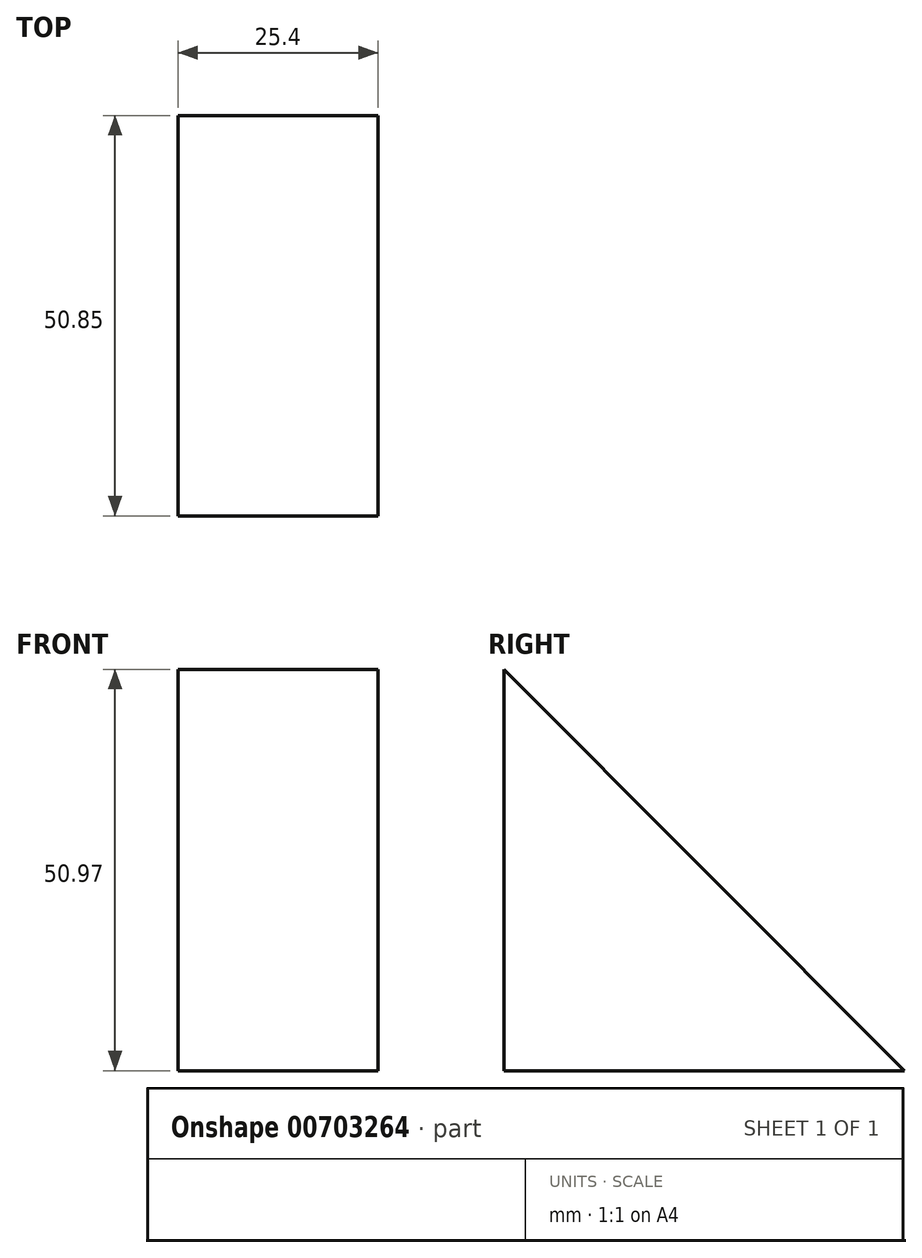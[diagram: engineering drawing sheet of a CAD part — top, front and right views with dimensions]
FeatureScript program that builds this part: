
annotation { "Feature Type Name" : "Feature", "Feature Type Description" : "" }
export const myFeature = defineFeature(function(context is Context, id is Id, definition is map)
    precondition{}
    {
        {
            var Q0;
            Q0=qCreatedBy(makeId("Right.planeOp"),FACE);
            var sketch = newSketch(context, id + "F0", { "sketchPlane" : qUnion([Q0])});
            skLineSegment(sketch, "E0", {"start": v(0, 0) * mm, "end": v(-50.85, 0) * mm});
            skLineSegment(sketch, "E1", {"start": v(-50.85, 0) * mm, "end": v(-50.85, 50.97) * mm});
            skLineSegment(sketch, "E2", {"start": v(-50.85, 50.97) * mm, "end": v(0, 0) * mm});
            skLineSegment(sketch, "E3", {"start": v(0, 0) * mm, "end": v(21.7, 0) * mm});
            skLineSegment(sketch, "E4", {"start": v(21.7, 0) * mm, "end": v(13.56, 0) * mm});
            skLineSegment(sketch, "E5", {"start": v(13.56, 0) * mm, "end": v(21.7, 0) * mm});
            skSolve(sketch);
        }
        {
            var Q0;
            Q0=makeQuery(id+"F0.imprint","IMPRINT",FACE,{"disambiguationData":[TD([[makeQuery(id+"F0.imprint","IMPRINT",EDGE,{"derivedFrom":sQuery(id+"F0.wireOp",EDGE,"E0")}),-1.0]])]});
            extrude(context, id + "F1", {"entities" : qUnion([Q0]), "depth" : 25.4 * mm, "offsetDistance" : 25.4 * mm});
        }
    });
